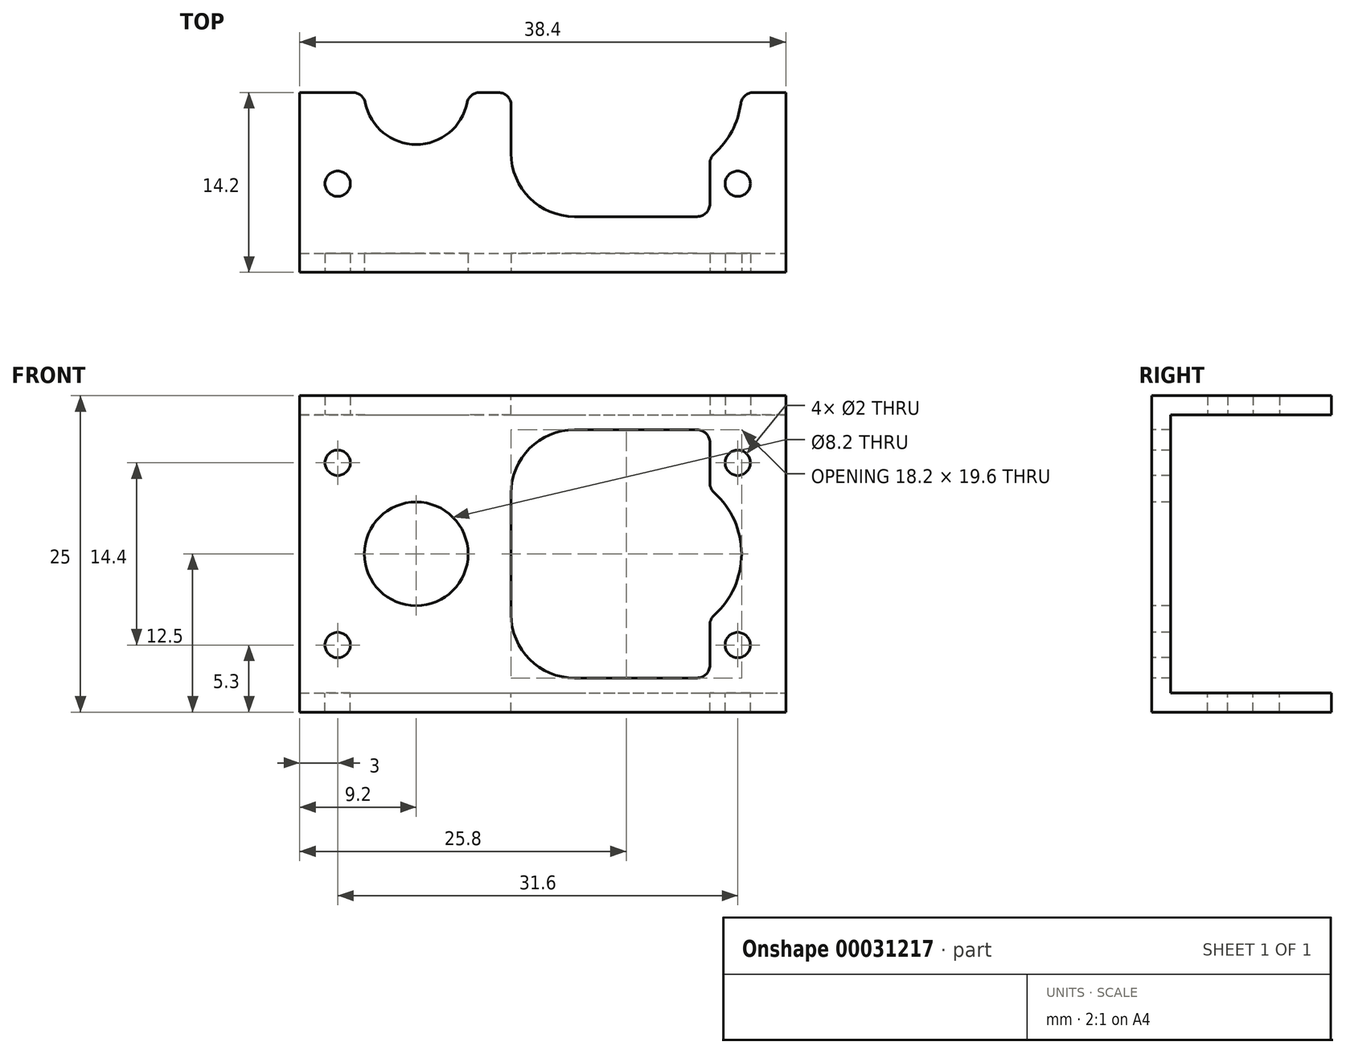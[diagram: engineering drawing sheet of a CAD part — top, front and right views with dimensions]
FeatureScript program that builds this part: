
annotation { "Feature Type Name" : "Feature", "Feature Type Description" : "" }
export const myFeature = defineFeature(function(context is Context, id is Id, definition is map)
    precondition{}
    {
        {
            var Q0;
            Q0=qCreatedBy(makeId("Top.planeOp"),FACE);
            var sketch = newSketch(context, id + "F0", { "sketchPlane" : qUnion([Q0])});
            skLineSegment(sketch, "E0.bottom", {"start": v(19.2, -14.2) * mm, "end": v(-19.2, -14.2) * mm});
            skLineSegment(sketch, "E0.top", {"start": v(19.2, 14.2) * mm, "end": v(-19.2, 14.2) * mm});
            skLineSegment(sketch, "E0.left", {"start": v(19.2, -14.2) * mm, "end": v(19.2, 14.2) * mm});
            skLineSegment(sketch, "E0.right", {"start": v(-19.2, -14.2) * mm, "end": v(-19.2, 14.2) * mm});
            skPoint(sketch, "E0.middle", {"position": v(0, 0) * mm});
            skCircle(sketch, "E1", {"center": v(-10, 0) * mm, "radius": 4.1 * mm});
            skCircle(sketch, "E2", {"center": v(-16.2, 7.2) * mm, "radius": 1 * mm});
            skCircle(sketch, "E3", {"center": v(15.4, 7.2) * mm, "radius": 1 * mm});
            skLineSegment(sketch, "E4.bottom", {"start": v(2.5, 9.8) * mm, "end": v(12.2, 9.8) * mm});
            skLineSegment(sketch, "E4.top", {"start": v(2.5, -9.8) * mm, "end": v(12.2, -9.8) * mm});
            skLineSegment(sketch, "E4.left", {"start": v(-2.5, 4.8) * mm, "end": v(-2.5, -4.8) * mm});
            skLineSegment(sketch, "E4.right", {"start": v(13.2, 8.8) * mm, "end": v(13.2, 5.6) * mm});
            skPoint(sketch, "E4.middle", {"position": v(5.35, 0) * mm});
            skPoint(sketch, "E5.visualSharp", {"position": v(-2.5, 9.8) * mm});
            skArc(sketch, "E5.filletArc", {"start": v(2.5, 9.8) * mm, "mid": v(-1.04, 8.34) * mm, "end": v(-2.5, 4.8) * mm});
            skPoint(sketch, "E6.visualSharp", {"position": v(-2.5, -9.8) * mm});
            skArc(sketch, "E6.filletArc", {"start": v(-2.5, -4.8) * mm, "mid": v(-1.04, -8.34) * mm, "end": v(2.5, -9.8) * mm});
            skPoint(sketch, "E7.visualSharp", {"position": v(13.2, 9.8) * mm});
            skArc(sketch, "E7.filletArc", {"start": v(13.2, 8.8) * mm, "mid": v(12.9, 9.5) * mm, "end": v(12.2, 9.8) * mm});
            skPoint(sketch, "E8.visualSharp", {"position": v(13.2, -9.8) * mm});
            skArc(sketch, "E8.filletArc", {"start": v(12.2, -9.8) * mm, "mid": v(12.9, -9.5) * mm, "end": v(13.2, -8.8) * mm});
            skCircle(sketch, "E9.MirrorC", {"center": v(-16.2, -7.2) * mm, "radius": 1 * mm});
            skCircle(sketch, "E10.MirrorC", {"center": v(15.4, -7.2) * mm, "radius": 1 * mm});
            skArc(sketch, "E11", {"start": v(13.53, -4.84) * mm, "mid": v(15.7, 0) * mm, "end": v(13.53, 4.84) * mm});
            skLineSegment(sketch, "E12.trimOffspring", {"start": v(13.2, -5.6) * mm, "end": v(13.2, -8.8) * mm});
            skPoint(sketch, "E13.visualSharp", {"position": v(13.2, 5.12) * mm});
            skArc(sketch, "E13.filletArc", {"start": v(13.2, 5.6) * mm, "mid": v(13.29, 5.18) * mm, "end": v(13.53, 4.84) * mm});
            skPoint(sketch, "E14.visualSharp", {"position": v(13.2, -5.12) * mm});
            skArc(sketch, "E14.filletArc", {"start": v(13.53, -4.84) * mm, "mid": v(13.29, -5.18) * mm, "end": v(13.2, -5.6) * mm});
            skSolve(sketch);
        }
        {
            var Q0;
            Q0=qSketchRegion(id+"F0",true);
            extrude(context, id + "F1", {"entities" : qUnion([Q0]), "depth" : 1.5 * mm});
        }
        {
            var Q0;
            Q0=makeQuery(id+"F1.opExtrude","CAP_FACE",FACE,{"disambiguationData":[OSD([sQuery(id+"F0.wireOp",EDGE,"E0.bottom"),sQuery(id+"F0.wireOp",EDGE,"E0.top"),sQuery(id+"F0.wireOp",EDGE,"E0.left"),sQuery(id+"F0.wireOp",EDGE,"E0.right"),sQuery(id+"F0.wireOp",EDGE,"E1"),sQuery(id+"F0.wireOp",EDGE,"E2"),sQuery(id+"F0.wireOp",EDGE,"E3"),sQuery(id+"F0.wireOp",EDGE,"E4.bottom"),sQuery(id+"F0.wireOp",EDGE,"E4.top"),sQuery(id+"F0.wireOp",EDGE,"E4.left"),sQuery(id+"F0.wireOp",EDGE,"E4.right"),sQuery(id+"F0.wireOp",EDGE,"E5.filletArc"),sQuery(id+"F0.wireOp",EDGE,"E6.filletArc"),sQuery(id+"F0.wireOp",EDGE,"E7.filletArc"),sQuery(id+"F0.wireOp",EDGE,"E8.filletArc"),sQuery(id+"F0.wireOp",EDGE,"E9.MirrorC"),sQuery(id+"F0.wireOp",EDGE,"E10.MirrorC"),sQuery(id+"F0.wireOp",EDGE,"E11"),sQuery(id+"F0.wireOp",EDGE,"E12.trimOffspring"),sQuery(id+"F0.wireOp",EDGE,"E13.filletArc"),sQuery(id+"F0.wireOp",EDGE,"E14.filletArc")])],"isStart":true});
            var sketch = newSketch(context, id + "F2", { "sketchPlane" : qUnion([Q0])});
            skLineSegment(sketch, "E15.bottom", {"start": v(-19.2, 14.2) * mm, "end": v(19.2, 14.2) * mm});
            skLineSegment(sketch, "E15.top", {"start": v(-19.2, 12.7) * mm, "end": v(19.2, 12.7) * mm});
            skLineSegment(sketch, "E15.left", {"start": v(-19.2, 14.2) * mm, "end": v(-19.2, 12.7) * mm});
            skLineSegment(sketch, "E15.right", {"start": v(19.2, 14.2) * mm, "end": v(19.2, 12.7) * mm});
            skSolve(sketch);
        }
        {
            var Q0;
            Q0 = qSketchRegion(id + "F2", true);
            extrude(context, id + "F3", {"entities" : qUnion([Q0]), "operationType" : NewBodyOperationType.ADD, "depth" : (29.3 - 3.8 - 3.5) * mm});
        }
        {
            var Q0;
            Q0=qCreatedBy(makeId("Top.planeOp"),FACE);
            cPlane(context, id + "F4", {"entities" : qUnion([Q0]), "cplaneType" : CPlaneType.OFFSET, "offset" : 11 * mm, "oppositeDirection" : true, "width" : 150 * mm, "height" : 150 * mm});
        }
        {
            var Q0;
            Q0=makeQuery(id+"F1.opExtrude","SWEPT_BODY",BODY,{"disambiguationData":[OSD([sQuery(id+"F0.wireOp",EDGE,"E0.bottom"),sQuery(id+"F0.wireOp",EDGE,"E0.top"),sQuery(id+"F0.wireOp",EDGE,"E0.left"),sQuery(id+"F0.wireOp",EDGE,"E0.right"),sQuery(id+"F0.wireOp",EDGE,"E1"),sQuery(id+"F0.wireOp",EDGE,"E2"),sQuery(id+"F0.wireOp",EDGE,"E3"),sQuery(id+"F0.wireOp",EDGE,"E4.bottom"),sQuery(id+"F0.wireOp",EDGE,"E4.top"),sQuery(id+"F0.wireOp",EDGE,"E4.left"),sQuery(id+"F0.wireOp",EDGE,"E4.right"),sQuery(id+"F0.wireOp",EDGE,"E5.filletArc"),sQuery(id+"F0.wireOp",EDGE,"E6.filletArc"),sQuery(id+"F0.wireOp",EDGE,"E7.filletArc"),sQuery(id+"F0.wireOp",EDGE,"E8.filletArc"),sQuery(id+"F0.wireOp",EDGE,"E9.MirrorC"),sQuery(id+"F0.wireOp",EDGE,"E10.MirrorC"),sQuery(id+"F0.wireOp",EDGE,"E11"),sQuery(id+"F0.wireOp",EDGE,"E12.trimOffspring"),sQuery(id+"F0.wireOp",EDGE,"E13.filletArc"),sQuery(id+"F0.wireOp",EDGE,"E14.filletArc")])]});
            var Q1;
            Q1=qCreatedBy(id+"F4.planeOp",FACE);
            mirror(context, id + "F5", {"operationType" : NewBodyOperationType.ADD, "entities" : qUnion([Q0]), "mirrorPlane" : qUnion([Q1])});
        }
        {
            var Q0;
            Q0=makeQuery(id+"F5.opPattern","COPY",FACE,{"derivedFrom":makeQuery(id+"F1.opExtrude","CAP_FACE",FACE,{"disambiguationData":[OSD([sQuery(id+"F0.wireOp",EDGE,"E0.bottom"),sQuery(id+"F0.wireOp",EDGE,"E0.top"),sQuery(id+"F0.wireOp",EDGE,"E0.left"),sQuery(id+"F0.wireOp",EDGE,"E0.right"),sQuery(id+"F0.wireOp",EDGE,"E1"),sQuery(id+"F0.wireOp",EDGE,"E2"),sQuery(id+"F0.wireOp",EDGE,"E3"),sQuery(id+"F0.wireOp",EDGE,"E4.bottom"),sQuery(id+"F0.wireOp",EDGE,"E4.top"),sQuery(id+"F0.wireOp",EDGE,"E4.left"),sQuery(id+"F0.wireOp",EDGE,"E4.right"),sQuery(id+"F0.wireOp",EDGE,"E5.filletArc"),sQuery(id+"F0.wireOp",EDGE,"E6.filletArc"),sQuery(id+"F0.wireOp",EDGE,"E7.filletArc"),sQuery(id+"F0.wireOp",EDGE,"E8.filletArc"),sQuery(id+"F0.wireOp",EDGE,"E9.MirrorC"),sQuery(id+"F0.wireOp",EDGE,"E10.MirrorC"),sQuery(id+"F0.wireOp",EDGE,"E11"),sQuery(id+"F0.wireOp",EDGE,"E12.trimOffspring"),sQuery(id+"F0.wireOp",EDGE,"E13.filletArc"),sQuery(id+"F0.wireOp",EDGE,"E14.filletArc")])],"isStart":false}),"instanceName":"1"});
            var sketch = newSketch(context, id + "F6", { "sketchPlane" : qUnion([Q0])});
            skLineSegment(sketch, "E16.bottom", {"start": v(-19.2, -14.2) * mm, "end": v(19.2, -14.2) * mm});
            skLineSegment(sketch, "E16.top", {"start": v(-19.2, 0) * mm, "end": v(19.2, 0) * mm});
            skLineSegment(sketch, "E16.left", {"start": v(-19.2, -14.2) * mm, "end": v(-19.2, 0) * mm});
            skLineSegment(sketch, "E16.right", {"start": v(19.2, -14.2) * mm, "end": v(19.2, 0) * mm});
            skSolve(sketch);
        }
        {
            var Q0;
            Q0 = qSketchRegion(id + "F6", true);
            extrude(context, id + "F7", {"entities" : qUnion([Q0]), "operationType" : NewBodyOperationType.REMOVE, "endBound" : BoundingType.THROUGH_ALL, "oppositeDirection" : true, "depth" : 25 * mm});
        }
        {
            var Q0;
            {var subQ0=makeQuery(id+"F3.boolean.opBoolean","MERGE",FACE,{"derivedFrom":[makeQuery(id+"F1.opExtrude","SWEPT_FACE",FACE,{"disambiguationData":[OSD([sQuery(id+"F0.wireOp",EDGE,"E0.bottom")])]}),makeQuery(id+"F3.opExtrude","SWEPT_FACE",FACE,{"disambiguationData":[OSD([sQuery(id+"F2.wireOp",EDGE,"E15.bottom")])]})]});Q0=makeQuery(id+"F5.boolean.opBoolean","MERGE",FACE,{"derivedFrom":[subQ0,makeQuery(id+"F5.opPattern","COPY",FACE,{"derivedFrom":subQ0,"instanceName":"1"})]});}
            var sketch = newSketch(context, id + "F8", { "sketchPlane" : qUnion([Q0])});
            skLineSegment(sketch, "E17", {"start": v(-19.2, -11) * mm, "end": v(19.2, -11) * mm, "construction": true});
            skCircle(sketch, "E18", {"center": v(-10, -11) * mm, "radius": 4.1 * mm});
            skCircle(sketch, "E19", {"center": v(-16.2, -3.8) * mm, "radius": 1 * mm});
            skCircle(sketch, "E20", {"center": v(15.4, -3.8) * mm, "radius": 1 * mm});
            skLineSegment(sketch, "E21.bottom", {"start": v(2.5, -1.2) * mm, "end": v(12.2, -1.2) * mm});
            skLineSegment(sketch, "E21.top", {"start": v(2.5, -20.8) * mm, "end": v(12.2, -20.8) * mm});
            skLineSegment(sketch, "E21.left", {"start": v(-2.5, -6.2) * mm, "end": v(-2.5, -15.8) * mm});
            skLineSegment(sketch, "E21.right", {"start": v(13.2, -2.2) * mm, "end": v(13.2, -5.4) * mm});
            skPoint(sketch, "E21.middle", {"position": v(5.35, -11) * mm});
            skPoint(sketch, "E22.visualSharp", {"position": v(-2.5, -1.2) * mm});
            skArc(sketch, "E22.filletArc", {"start": v(2.5, -1.2) * mm, "mid": v(-1.04, -2.66) * mm, "end": v(-2.5, -6.2) * mm});
            skPoint(sketch, "E23.visualSharp", {"position": v(-2.5, -20.8) * mm});
            skArc(sketch, "E23.filletArc", {"start": v(-2.5, -15.8) * mm, "mid": v(-1.04, -19.34) * mm, "end": v(2.5, -20.8) * mm});
            skPoint(sketch, "E24.visualSharp", {"position": v(13.2, -1.2) * mm});
            skArc(sketch, "E24.filletArc", {"start": v(13.2, -2.2) * mm, "mid": v(12.9, -1.5) * mm, "end": v(12.2, -1.2) * mm});
            skPoint(sketch, "E25.visualSharp", {"position": v(13.2, -20.8) * mm});
            skArc(sketch, "E25.filletArc", {"start": v(12.2, -20.8) * mm, "mid": v(12.9, -20.5) * mm, "end": v(13.2, -19.8) * mm});
            skArc(sketch, "E26", {"start": v(13.53, -15.84) * mm, "mid": v(15.7, -11) * mm, "end": v(13.53, -6.16) * mm});
            skLineSegment(sketch, "E27.trimOffspring", {"start": v(13.2, -16.6) * mm, "end": v(13.2, -19.8) * mm});
            skPoint(sketch, "E28.visualSharp", {"position": v(13.2, -5.88) * mm});
            skArc(sketch, "E28.filletArc", {"start": v(13.2, -5.4) * mm, "mid": v(13.29, -5.82) * mm, "end": v(13.53, -6.16) * mm});
            skPoint(sketch, "E29.visualSharp", {"position": v(13.2, -16.12) * mm});
            skArc(sketch, "E29.filletArc", {"start": v(13.53, -15.84) * mm, "mid": v(13.29, -16.18) * mm, "end": v(13.2, -16.6) * mm});
            skCircle(sketch, "E30.MirrorC", {"center": v(-16.2, -18.2) * mm, "radius": 1 * mm});
            skCircle(sketch, "E31.MirrorC", {"center": v(15.4, -18.2) * mm, "radius": 1 * mm});
            skSolve(sketch);
        }
        {
            var Q0;
            Q0 = qSketchRegion(id + "F8", true);
            extrude(context, id + "F9", {"entities" : qUnion([Q0]), "operationType" : NewBodyOperationType.REMOVE, "endBound" : BoundingType.UP_TO_NEXT, "oppositeDirection" : true, "depth" : 25 * mm});
        }
        {
            var Q0;
            Q0=makeQuery(id+"F7.boolean.opBoolean","COPY",EDGE,{"disambiguationData":[OD(0.0)],"derivedFrom":makeQuery(id+"F7.opExtrude","SWEPT_EDGE",EDGE,{"disambiguationData":[OSD([sQuery(id+"F0.wireOp",EDGE,"E0.right"),sQuery(id+"F6.wireOp",EDGE,"E16.top"),sQuery(id+"F6.wireOp",EDGE,"E16.left")])]})});
            var Q1;
            Q1=makeQuery(id+"F7.boolean.opBoolean","COPY",EDGE,{"disambiguationData":[OD(1.0)],"derivedFrom":makeQuery(id+"F7.opExtrude","SWEPT_EDGE",EDGE,{"disambiguationData":[OSD([sQuery(id+"F0.wireOp",EDGE,"E0.right"),sQuery(id+"F6.wireOp",EDGE,"E16.top"),sQuery(id+"F6.wireOp",EDGE,"E16.left")])]})});
            var Q2;
            Q2=makeQuery(id+"F7.boolean.opBoolean","INTERSECT",EDGE,{"disambiguationData":[OD(1.0)],"derivedFrom":[makeQuery(id+"F1.opExtrude","SWEPT_FACE",FACE,{"disambiguationData":[OSD([sQuery(id+"F0.wireOp",EDGE,"E1")])]}),makeQuery(id+"F7.opExtrude","SWEPT_FACE",FACE,{"disambiguationData":[OSD([sQuery(id+"F6.wireOp",EDGE,"E16.top")])]})]});
            var Q3;
            Q3=makeQuery(id+"F7.boolean.opBoolean","INTERSECT",EDGE,{"disambiguationData":[OD(1.0)],"derivedFrom":[makeQuery(id+"F5.opPattern","COPY",FACE,{"derivedFrom":makeQuery(id+"F1.opExtrude","SWEPT_FACE",FACE,{"disambiguationData":[OSD([sQuery(id+"F0.wireOp",EDGE,"E1")])]}),"instanceName":"1"}),makeQuery(id+"F7.opExtrude","SWEPT_FACE",FACE,{"disambiguationData":[OSD([sQuery(id+"F6.wireOp",EDGE,"E16.top")])]})]});
            var Q4;
            Q4=makeQuery(id+"F7.boolean.opBoolean","INTERSECT",EDGE,{"disambiguationData":[OD(0.0)],"derivedFrom":[makeQuery(id+"F5.opPattern","COPY",FACE,{"derivedFrom":makeQuery(id+"F1.opExtrude","SWEPT_FACE",FACE,{"disambiguationData":[OSD([sQuery(id+"F0.wireOp",EDGE,"E1")])]}),"instanceName":"1"}),makeQuery(id+"F7.opExtrude","SWEPT_FACE",FACE,{"disambiguationData":[OSD([sQuery(id+"F6.wireOp",EDGE,"E16.top")])]})]});
            var Q5;
            Q5=makeQuery(id+"F7.boolean.opBoolean","INTERSECT",EDGE,{"derivedFrom":[makeQuery(id+"F5.opPattern","COPY",FACE,{"derivedFrom":makeQuery(id+"F1.opExtrude","SWEPT_FACE",FACE,{"disambiguationData":[OSD([sQuery(id+"F0.wireOp",EDGE,"E4.left")])]}),"instanceName":"1"}),makeQuery(id+"F7.opExtrude","SWEPT_FACE",FACE,{"disambiguationData":[OSD([sQuery(id+"F6.wireOp",EDGE,"E16.top")])]})]});
            var Q6;
            Q6=makeQuery(id+"F7.boolean.opBoolean","INTERSECT",EDGE,{"disambiguationData":[OD(0.0)],"derivedFrom":[makeQuery(id+"F1.opExtrude","SWEPT_FACE",FACE,{"disambiguationData":[OSD([sQuery(id+"F0.wireOp",EDGE,"E1")])]}),makeQuery(id+"F7.opExtrude","SWEPT_FACE",FACE,{"disambiguationData":[OSD([sQuery(id+"F6.wireOp",EDGE,"E16.top")])]})]});
            var Q7;
            Q7=makeQuery(id+"F7.boolean.opBoolean","INTERSECT",EDGE,{"derivedFrom":[makeQuery(id+"F5.opPattern","COPY",FACE,{"derivedFrom":makeQuery(id+"F1.opExtrude","SWEPT_FACE",FACE,{"disambiguationData":[OSD([sQuery(id+"F0.wireOp",EDGE,"E11")])]}),"instanceName":"1"}),makeQuery(id+"F7.opExtrude","SWEPT_FACE",FACE,{"disambiguationData":[OSD([sQuery(id+"F6.wireOp",EDGE,"E16.top")])]})]});
            var Q8;
            Q8=makeQuery(id+"F7.boolean.opBoolean","INTERSECT",EDGE,{"derivedFrom":[makeQuery(id+"F1.opExtrude","SWEPT_FACE",FACE,{"disambiguationData":[OSD([sQuery(id+"F0.wireOp",EDGE,"E11")])]}),makeQuery(id+"F7.opExtrude","SWEPT_FACE",FACE,{"disambiguationData":[OSD([sQuery(id+"F6.wireOp",EDGE,"E16.top")])]})]});
            var Q9;
            Q9=makeQuery(id+"F7.boolean.opBoolean","COPY",EDGE,{"disambiguationData":[OD(0.0)],"derivedFrom":makeQuery(id+"F7.opExtrude","SWEPT_EDGE",EDGE,{"disambiguationData":[OSD([sQuery(id+"F0.wireOp",EDGE,"E0.left"),sQuery(id+"F6.wireOp",EDGE,"E16.top"),sQuery(id+"F6.wireOp",EDGE,"E16.right")])]})});
            var Q10;
            Q10=makeQuery(id+"F7.boolean.opBoolean","INTERSECT",EDGE,{"derivedFrom":[makeQuery(id+"F1.opExtrude","SWEPT_FACE",FACE,{"disambiguationData":[OSD([sQuery(id+"F0.wireOp",EDGE,"E4.left")])]}),makeQuery(id+"F7.opExtrude","SWEPT_FACE",FACE,{"disambiguationData":[OSD([sQuery(id+"F6.wireOp",EDGE,"E16.top")])]})]});
            var Q11;
            Q11=makeQuery(id+"F7.boolean.opBoolean","COPY",EDGE,{"disambiguationData":[OD(1.0)],"derivedFrom":makeQuery(id+"F7.opExtrude","SWEPT_EDGE",EDGE,{"disambiguationData":[OSD([sQuery(id+"F0.wireOp",EDGE,"E0.left"),sQuery(id+"F6.wireOp",EDGE,"E16.top"),sQuery(id+"F6.wireOp",EDGE,"E16.right")])]})});
            fillet(context, id + "F10", {"entities" : qUnion([Q0, Q1, Q2, Q3, Q4, Q5, Q6, Q7, Q8, Q9, Q10, Q11]), "radius" : 1 * mm, "tangentPropagation" : true, "allowEdgeOverflow" : false});
        }
    });
